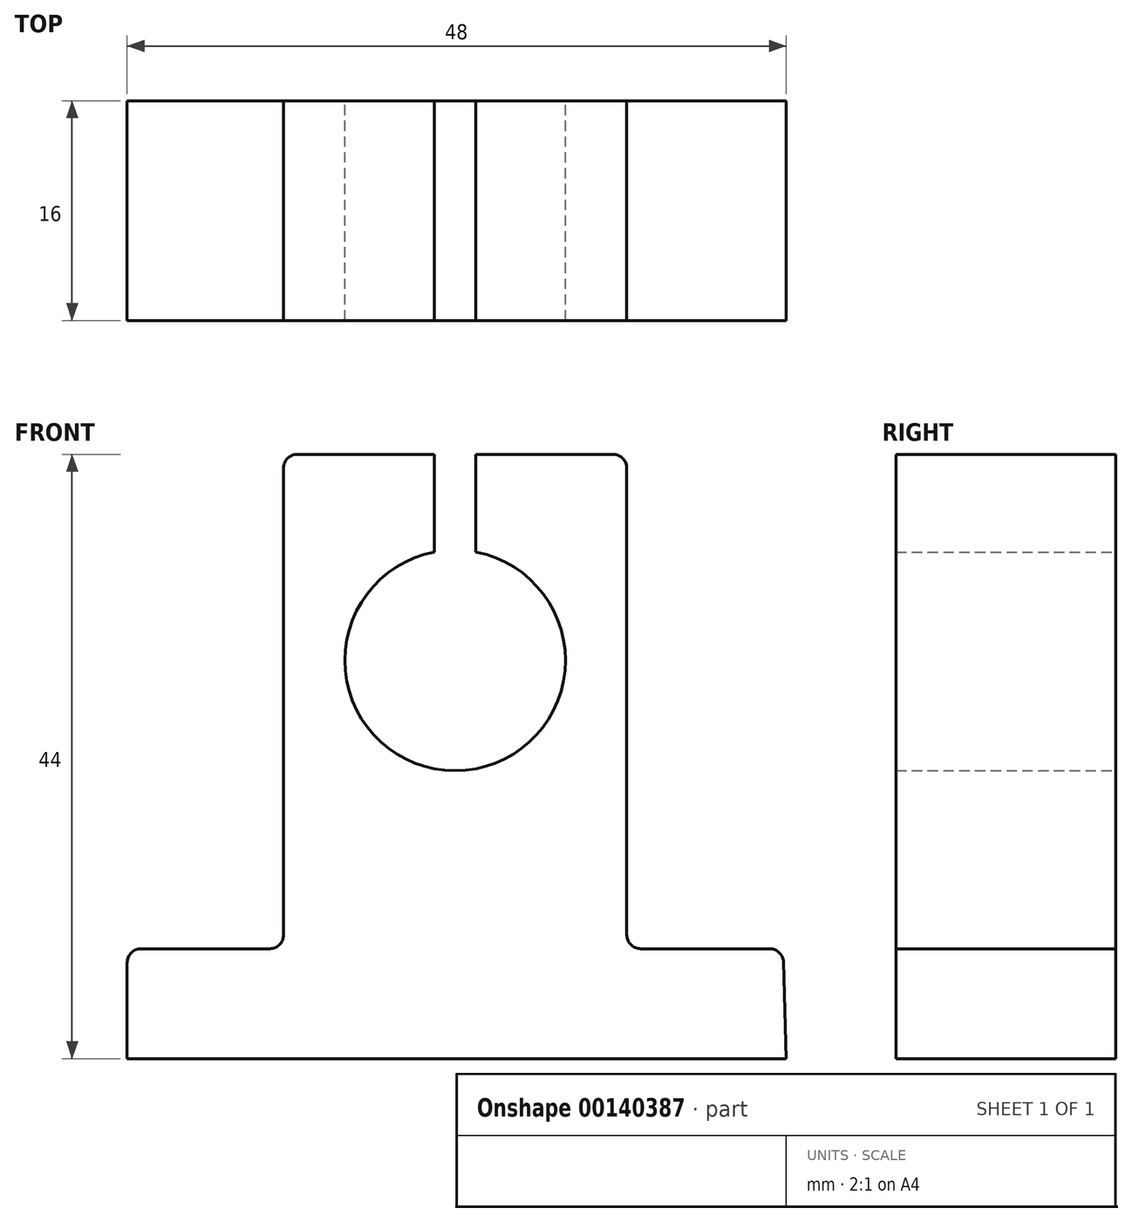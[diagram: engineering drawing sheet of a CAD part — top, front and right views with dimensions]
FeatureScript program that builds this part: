
annotation { "Feature Type Name" : "Feature", "Feature Type Description" : "" }
export const myFeature = defineFeature(function(context is Context, id is Id, definition is map)
    precondition{}
    {
        {
            var Q0;
            Q0=qCreatedBy(makeId("Front.planeOp"),FACE);
            var sketch = newSketch(context, id + "F0", { "sketchPlane" : qUnion([Q0])});
            skLineSegment(sketch, "E0", {"start": v(24.11, -10.22) * mm, "end": v(-23.89, -10.22) * mm});
            skLineSegment(sketch, "E1", {"start": v(-23.89, -10.22) * mm, "end": v(-23.89, -3.22) * mm});
            skLineSegment(sketch, "E2", {"start": v(-22.89, -2.22) * mm, "end": v(-13.5, -2.22) * mm});
            skLineSegment(sketch, "E3", {"start": v(-12.5, -1.22) * mm, "end": v(-12.5, 32.78) * mm});
            skLineSegment(sketch, "E4", {"start": v(-11.5, 33.78) * mm, "end": v(-1.5, 33.78) * mm});
            skLineSegment(sketch, "E5", {"start": v(12.5, 32.78) * mm, "end": v(12.5, -1.22) * mm});
            skLineSegment(sketch, "E6", {"start": v(13.5, -2.22) * mm, "end": v(22.92, -2.22) * mm});
            skLineSegment(sketch, "E7", {"start": v(23.91, -3.2) * mm, "end": v(24.11, -10.22) * mm});
            skLineSegment(sketch, "E8", {"start": v(0, 25.14) * mm, "end": v(0, -5.96) * mm, "construction": true});
            skPoint(sketch, "E9.visualSharp", {"position": v(-12.5, 33.78) * mm});
            skArc(sketch, "E9.filletArc", {"start": v(-11.5, 33.78) * mm, "mid": v(-12.2, 33.49) * mm, "end": v(-12.5, 32.78) * mm});
            skPoint(sketch, "E10.visualSharp", {"position": v(12.5, 33.78) * mm});
            skArc(sketch, "E10.filletArc", {"start": v(12.5, 32.78) * mm, "mid": v(12.2, 33.49) * mm, "end": v(11.5, 33.78) * mm});
            skPoint(sketch, "E11.visualSharp", {"position": v(-12.5, -2.22) * mm});
            skArc(sketch, "E11.filletArc", {"start": v(-13.5, -2.22) * mm, "mid": v(-12.8, -1.93) * mm, "end": v(-12.5, -1.22) * mm});
            skPoint(sketch, "E12.visualSharp", {"position": v(12.5, -2.22) * mm});
            skArc(sketch, "E12.filletArc", {"start": v(12.5, -1.22) * mm, "mid": v(12.8, -1.93) * mm, "end": v(13.5, -2.22) * mm});
            skArc(sketch, "E13", {"start": v(-1.5, 26.67) * mm, "mid": v(0, 10.75) * mm, "end": v(1.5, 26.67) * mm});
            skLineSegment(sketch, "E14", {"start": v(-1.5, 41.47) * mm, "end": v(-1.5, 26.67) * mm});
            skLineSegment(sketch, "E15.MirrorCS", {"start": v(1.5, 41.47) * mm, "end": v(1.5, 26.67) * mm});
            skLineSegment(sketch, "E16.trimOffspring", {"start": v(1.5, 33.78) * mm, "end": v(11.5, 33.78) * mm});
            skPoint(sketch, "E17.orphan", {"position": v(-1.5, 19.09) * mm});
            skPoint(sketch, "E18.orphan", {"position": v(1.5, 19.09) * mm});
            skPoint(sketch, "E19.visualSharp", {"position": v(-23.89, -2.22) * mm});
            skArc(sketch, "E19.filletArc", {"start": v(-22.89, -2.22) * mm, "mid": v(-23.6, -2.51) * mm, "end": v(-23.89, -3.22) * mm});
            skPoint(sketch, "E20.visualSharp", {"position": v(23.89, -2.22) * mm});
            skArc(sketch, "E20.filletArc", {"start": v(23.91, -3.2) * mm, "mid": v(23.61, -2.5) * mm, "end": v(22.92, -2.22) * mm});
            skSolve(sketch);
        }
        {
            var Q0;
            Q0 = qSketchRegion(id + "F0", true);
            extrude(context, id + "F1", {"entities" : qUnion([Q0]), "endBound" : BoundingType.SYMMETRIC, "depth" : 16 * mm});
        }
    });
